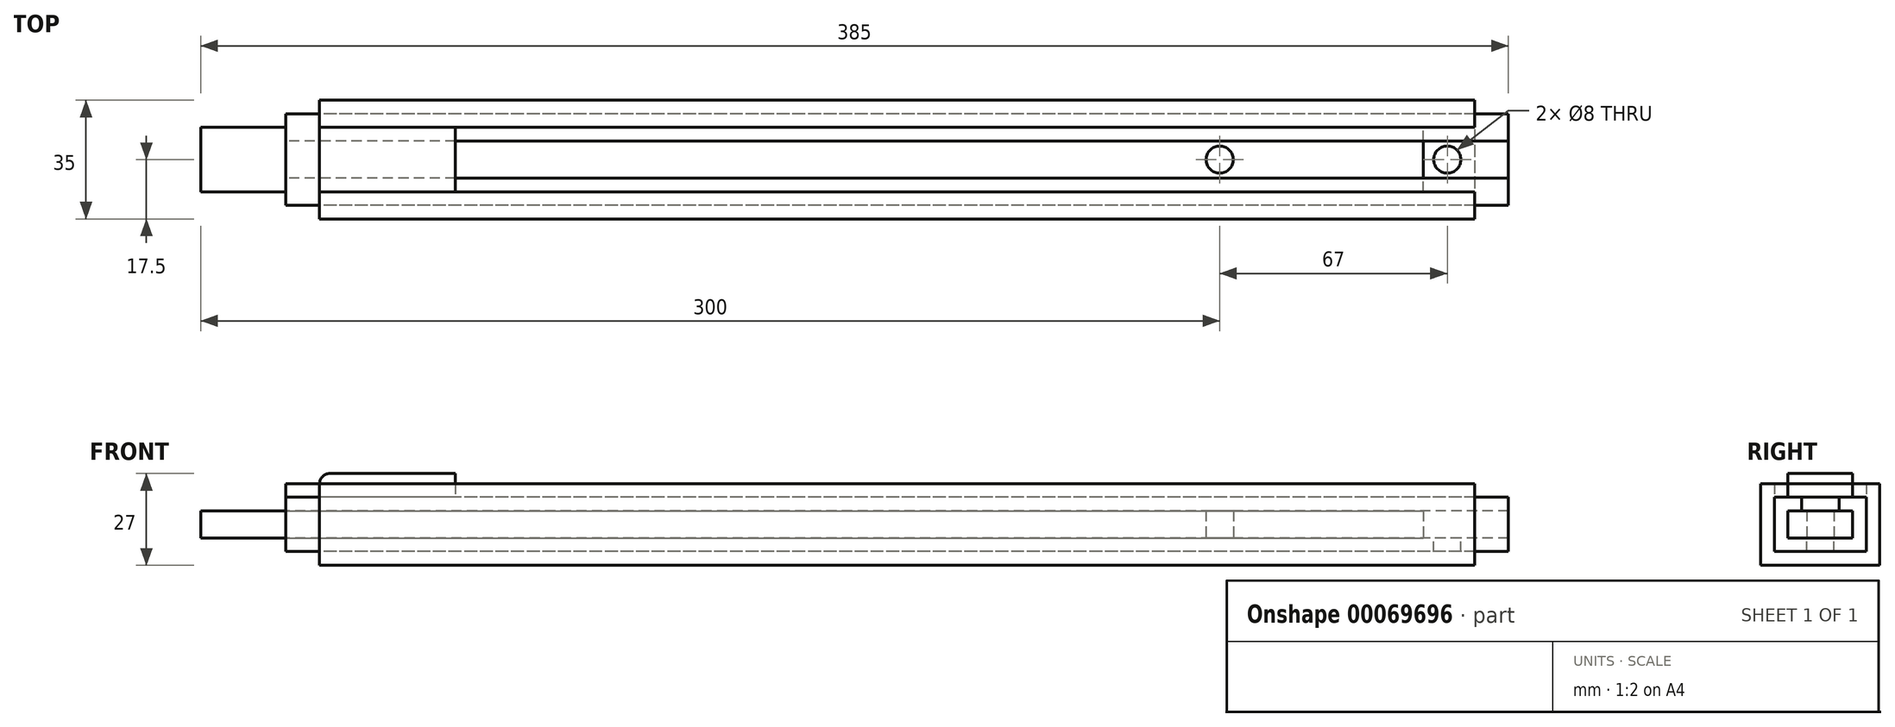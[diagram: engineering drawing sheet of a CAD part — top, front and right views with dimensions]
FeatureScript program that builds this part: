
annotation { "Feature Type Name" : "Feature", "Feature Type Description" : "" }
export const myFeature = defineFeature(function(context is Context, id is Id, definition is map)
    precondition{}
    {
        {
            var Q0;
            Q0=qCreatedBy(makeId("Top.planeOp"),FACE);
            var sketch = newSketch(context, id + "F0", { "sketchPlane" : qUnion([Q0])});
            skLineSegment(sketch, "E0.bottom", {"start": v(0, 0) * mm, "end": v(360, 0) * mm});
            skLineSegment(sketch, "E0.top", {"start": v(0, 19) * mm, "end": v(360, 19) * mm});
            skLineSegment(sketch, "E0.left", {"start": v(0, 0) * mm, "end": v(0, 19) * mm});
            skLineSegment(sketch, "E0.right", {"start": v(360, 0) * mm, "end": v(360, 19) * mm});
            skCircle(sketch, "E1", {"center": v(300, 9.5) * mm, "radius": 4 * mm});
            skPoint(sketch, "E1.centerSnap0", {"position": v(360, 9.5) * mm});
            skSolve(sketch);
        }
        {
            var Q0;
            Q0=makeQuery(id+"F0.imprint","IMPRINT",FACE,{"disambiguationData":[TD([[makeQuery(id+"F0.imprint","IMPRINT",EDGE,{"derivedFrom":sQuery(id+"F0.wireOp",EDGE,"E0.bottom")}),1.0]])]});
            extrude(context, id + "F1", {"entities" : qUnion([Q0]), "depth" : 8 * mm});
        }
        {
            var Q0;
            Q0=makeQuery(id+"F1.opExtrude","SWEPT_FACE",FACE,{"disambiguationData":[OSD([sQuery(id+"F0.wireOp",EDGE,"E0.left")])]});
            cPlane(context, id + "F2", {"entities" : qUnion([Q0]), "cplaneType" : CPlaneType.OFFSET, "offset" : 25 * mm, "oppositeDirection" : true, "width" : 150 * mm, "height" : 150 * mm});
        }
        {
            var Q0;
            Q0=qCreatedBy(id+"F2.planeOp",FACE);
            var sketch = newSketch(context, id + "F3", { "sketchPlane" : qUnion([Q0])});
            skLineSegment(sketch, "E2.0.0", {"start": v(-19, 0) * mm, "end": v(0, 0) * mm});
            skLineSegment(sketch, "E2.0.1", {"start": v(0, 0) * mm, "end": v(0, 8) * mm});
            skLineSegment(sketch, "E2.0.2", {"start": v(0, 8) * mm, "end": v(-19, 8) * mm});
            skLineSegment(sketch, "E2.0.3", {"start": v(-19, 8) * mm, "end": v(-19, 0) * mm});
            skLineSegment(sketch, "E3.bottom", {"start": v(-23, -4) * mm, "end": v(4, -4) * mm});
            skLineSegment(sketch, "E3.top", {"start": v(-23, 12) * mm, "end": v(-15, 12) * mm});
            skLineSegment(sketch, "E3.left", {"start": v(-23, -4) * mm, "end": v(-23, 12) * mm});
            skLineSegment(sketch, "E3.right", {"start": v(4, -4) * mm, "end": v(4, 12) * mm});
            skLineSegment(sketch, "E4", {"start": v(-15, 12) * mm, "end": v(-15, 8) * mm});
            skLineSegment(sketch, "E5", {"start": v(-4, 12) * mm, "end": v(-4, 8) * mm});
            skLineSegment(sketch, "E6.trimOffspring", {"start": v(-4, 12) * mm, "end": v(4, 12) * mm});
            skSolve(sketch);
        }
        {
            var Q0;
            Q0=makeQuery(id+"F3.imprint","IMPRINT",FACE,{"disambiguationData":[TD([[makeQuery(id+"F3.imprint","IMPRINT",EDGE,{"derivedFrom":sQuery(id+"F3.wireOp",EDGE,"E2.0.0")}),-1.0]])]});
            extrude(context, id + "F4", {"entities" : qUnion([Q0]), "oppositeDirection" : true, "depth" : 360 * mm});
        }
        {
            var Q0;
            Q0=makeQuery(id+"F4.opExtrude","CAP_FACE",FACE,{"disambiguationData":[OSD([sQuery(id+"F3.wireOp",EDGE,"E2.0.0"),sQuery(id+"F3.wireOp",EDGE,"E2.0.1"),sQuery(id+"F3.wireOp",EDGE,"E2.0.2"),sQuery(id+"F3.wireOp",EDGE,"E2.0.3"),sQuery(id+"F3.wireOp",EDGE,"E3.bottom"),sQuery(id+"F3.wireOp",EDGE,"E3.top"),sQuery(id+"F3.wireOp",EDGE,"E3.left"),sQuery(id+"F3.wireOp",EDGE,"E3.right"),sQuery(id+"F3.wireOp",EDGE,"E4"),sQuery(id+"F3.wireOp",EDGE,"E5"),sQuery(id+"F3.wireOp",EDGE,"E6.trimOffspring")])],"isStart":true});
            cPlane(context, id + "F5", {"entities" : qUnion([Q0]), "cplaneType" : CPlaneType.OFFSET, "offset" : 10 * mm, "oppositeDirection" : true, "width" : 150 * mm, "height" : 150 * mm});
        }
        {
            var Q0;
            Q0=qCreatedBy(id+"F5.planeOp",FACE);
            var sketch = newSketch(context, id + "F6", { "sketchPlane" : qUnion([Q0])});
            skLineSegment(sketch, "E7.bottom", {"start": v(-27, -8) * mm, "end": v(8, -8) * mm});
            skLineSegment(sketch, "E7.top", {"start": v(-27, 16) * mm, "end": v(-19, 16) * mm});
            skLineSegment(sketch, "E7.left", {"start": v(-27, -8) * mm, "end": v(-27, 16) * mm});
            skLineSegment(sketch, "E7.right", {"start": v(8, -8) * mm, "end": v(8, 16) * mm});
            skLineSegment(sketch, "E8", {"start": v(0, 16) * mm, "end": v(0, 11.98) * mm});
            skLineSegment(sketch, "E9.0", {"start": v(-19, 8) * mm, "end": v(-19, 0) * mm});
            skLineSegment(sketch, "E10", {"start": v(-19, 16) * mm, "end": v(-19, 11.9) * mm});
            skLineSegment(sketch, "E11.trimOffspring", {"start": v(0, 16) * mm, "end": v(8, 16) * mm});
            skLineSegment(sketch, "E12.0", {"start": v(-23, -4) * mm, "end": v(-23, 12) * mm});
            skLineSegment(sketch, "E13.0", {"start": v(-23, 12) * mm, "end": v(-15, 12) * mm});
            skLineSegment(sketch, "E14.0", {"start": v(-23, -4) * mm, "end": v(4, -4) * mm});
            skLineSegment(sketch, "E15.0", {"start": v(4, -4) * mm, "end": v(4, 12) * mm});
            skLineSegment(sketch, "E16.0", {"start": v(-4, 12) * mm, "end": v(4, 12) * mm});
            skSolve(sketch);
        }
        {
            var Q0;
            Q0=makeQuery(id+"F6.imprint","IMPRINT",FACE,{"disambiguationData":[TD([[makeQuery(id+"F6.imprint","IMPRINT",EDGE,{"derivedFrom":sQuery(id+"F6.wireOp",EDGE,"E7.bottom")}),1.0]])]});
            extrude(context, id + "F7", {"entities" : qUnion([Q0]), "oppositeDirection" : true, "depth" : 340 * mm});
        }
        {
            var Q0;
            Q0=makeQuery(id+"F4.opExtrude","SWEPT_FACE",FACE,{"disambiguationData":[OSD([sQuery(id+"F3.wireOp",EDGE,"E3.top")])]});
            var sketch = newSketch(context, id + "F8", { "sketchPlane" : qUnion([Q0])});
            skLineSegment(sketch, "E17.0.0", {"start": v(25, 23) * mm, "end": v(25, 15) * mm});
            skLineSegment(sketch, "E17.0.1", {"start": v(25, 15) * mm, "end": v(385, 15) * mm});
            skLineSegment(sketch, "E17.0.2", {"start": v(385, 15) * mm, "end": v(385, 23) * mm});
            skLineSegment(sketch, "E17.0.3", {"start": v(385, 23) * mm, "end": v(25, 23) * mm});
            skLineSegment(sketch, "E18.0.0", {"start": v(25, 4) * mm, "end": v(25, -4) * mm});
            skLineSegment(sketch, "E18.0.1", {"start": v(25, -4) * mm, "end": v(385, -4) * mm});
            skLineSegment(sketch, "E18.0.2", {"start": v(385, -4) * mm, "end": v(385, 4) * mm});
            skLineSegment(sketch, "E18.0.3", {"start": v(385, 4) * mm, "end": v(25, 4) * mm});
            skLineSegment(sketch, "E19.0.0", {"start": v(35, 0) * mm, "end": v(35, -8) * mm});
            skLineSegment(sketch, "E19.0.1", {"start": v(35, -8) * mm, "end": v(375, -8) * mm});
            skLineSegment(sketch, "E19.0.2", {"start": v(375, -8) * mm, "end": v(375, 0) * mm});
            skLineSegment(sketch, "E19.0.3", {"start": v(375, 0) * mm, "end": v(35, 0) * mm});
            skLineSegment(sketch, "E20.0.0", {"start": v(35, 27) * mm, "end": v(35, 19) * mm});
            skLineSegment(sketch, "E20.0.1", {"start": v(35, 19) * mm, "end": v(375, 19) * mm});
            skLineSegment(sketch, "E20.0.2", {"start": v(375, 19) * mm, "end": v(375, 27) * mm});
            skLineSegment(sketch, "E20.0.3", {"start": v(375, 27) * mm, "end": v(35, 27) * mm});
            skLineSegment(sketch, "E21", {"start": v(75, 19) * mm, "end": v(75, 0) * mm});
            skLineSegment(sketch, "E22", {"start": v(25, 15) * mm, "end": v(25, 4) * mm});
            skSolve(sketch);
        }
        {
            var Q0;
            {var subQ5=sQuery(id+"F8.wireOp",EDGE,"E17.0.0");Q0=makeQuery(id+"F8.imprint","IMPRINT",FACE,{"disambiguationData":[TD([[makeQuery(id+"F8.imprint","IMPRINT",EDGE,{"derivedFrom":subQ5}),1.0]])]});}
            var Q1;
            {var subQ0=sQuery(id+"F8.wireOp",EDGE,"E22");Q1=makeQuery(id+"F8.imprint","IMPRINT",FACE,{"disambiguationData":[TD([[makeQuery(id+"F8.imprint","IMPRINT",EDGE,{"derivedFrom":subQ0}),1.0]])]});}
            var Q2;
            {var subQ6=sQuery(id+"F8.wireOp",EDGE,"E18.0.0");Q2=makeQuery(id+"F8.imprint","IMPRINT",FACE,{"disambiguationData":[TD([[makeQuery(id+"F8.imprint","IMPRINT",EDGE,{"derivedFrom":subQ6}),1.0]])]});}
            extrude(context, id + "F9", {"entities" : qUnion([Q0, Q1, Q2]), "depth" : 4 * mm});
        }
        {
            var Q0;
            Q0=makeQuery(id+"F7.opExtrude","SWEPT_FACE",FACE,{"disambiguationData":[OSD([sQuery(id+"F6.wireOp",EDGE,"E7.top")])]});
            var sketch = newSketch(context, id + "F10", { "sketchPlane" : qUnion([Q0])});
            skLineSegment(sketch, "E23.0.0", {"start": v(35, 27) * mm, "end": v(35, 19) * mm});
            skLineSegment(sketch, "E23.0.1", {"start": v(35, 19) * mm, "end": v(375, 19) * mm});
            skLineSegment(sketch, "E23.0.2", {"start": v(375, 19) * mm, "end": v(375, 27) * mm});
            skLineSegment(sketch, "E23.0.3", {"start": v(375, 27) * mm, "end": v(35, 27) * mm});
            skLineSegment(sketch, "E24.0.0", {"start": v(35, 0) * mm, "end": v(35, -8) * mm});
            skLineSegment(sketch, "E24.0.1", {"start": v(35, -8) * mm, "end": v(375, -8) * mm});
            skLineSegment(sketch, "E24.0.2", {"start": v(375, -8) * mm, "end": v(375, 0) * mm});
            skLineSegment(sketch, "E24.0.3", {"start": v(375, 0) * mm, "end": v(35, 0) * mm});
            skLineSegment(sketch, "E25.0", {"start": v(75, 19) * mm, "end": v(75, 0) * mm});
            skLineSegment(sketch, "E26.bottom", {"start": v(35, -8) * mm, "end": v(75, -8) * mm});
            skLineSegment(sketch, "E26.top", {"start": v(35, 27) * mm, "end": v(75, 27) * mm});
            skLineSegment(sketch, "E26.left", {"start": v(35, -8) * mm, "end": v(35, 27) * mm});
            skLineSegment(sketch, "E26.right", {"start": v(75, -8) * mm, "end": v(75, 27) * mm});
            skSolve(sketch);
        }
        {
            var Q0;
            {var subQ5=sQuery(id+"F10.wireOp",EDGE,"E26.top");Q0=makeQuery(id+"F10.imprint","IMPRINT",FACE,{"disambiguationData":[TD([[makeQuery(id+"F10.imprint","IMPRINT",EDGE,{"derivedFrom":subQ5}),1.0]])]});}
            var Q1;
            {var subQ0=sQuery(id+"F10.wireOp",EDGE,"E26.left");var subQ1=sQuery(id+"F10.wireOp",EDGE,"E23.0.1");var subQ2=makeQuery(id+"F10.imprint","INTERSECT",VERTEX,{"derivedFrom":[subQ1,subQ0]});Q1=makeQuery(id+"F10.imprint","IMPRINT",FACE,{"disambiguationData":[TD([[makeQuery(id+"F10.imprint","IMPRINT",EDGE,{"disambiguationData":[TD([[subQ2,1.0]])],"derivedFrom":subQ1}),1.0]])]});}
            var Q2;
            {var subQ5=sQuery(id+"F10.wireOp",EDGE,"E26.bottom");Q2=makeQuery(id+"F10.imprint","IMPRINT",FACE,{"disambiguationData":[TD([[makeQuery(id+"F10.imprint","IMPRINT",EDGE,{"derivedFrom":subQ5}),1.0]])]});}
            extrude(context, id + "F11", {"entities" : qUnion([Q0, Q1, Q2]), "depth" : 3 * mm});
        }
        {
            var Q0;
            Q0=makeQuery(id+"F11.opExtrude","CAP_EDGE",EDGE,{"disambiguationData":[OSD([sQuery(id+"F10.wireOp",EDGE,"E26.bottom")])],"isStart":false});
            var Q1;
            Q1=makeQuery(id+"F11.opExtrude","CAP_EDGE",EDGE,{"disambiguationData":[OSD([sQuery(id+"F10.wireOp",EDGE,"E26.left")])],"isStart":false});
            var Q2;
            Q2=makeQuery(id+"F11.opExtrude","CAP_EDGE",EDGE,{"disambiguationData":[OSD([sQuery(id+"F10.wireOp",EDGE,"E26.top")])],"isStart":false});
            var Q3;
            Q3=makeQuery(id+"F11.opExtrude","CAP_EDGE",EDGE,{"disambiguationData":[OSD([sQuery(id+"F10.wireOp",EDGE,"E26.right")])],"isStart":false});
            fillet(context, id + "F12", {"entities" : qUnion([Q0, Q1, Q2, Q3]), "radius" : 3 * mm, "tangentPropagation" : true, "allowEdgeOverflow" : false});
        }
        {
            var Q0;
            Q0=makeQuery(id+"F4.opExtrude","SWEPT_FACE",FACE,{"disambiguationData":[OSD([sQuery(id+"F3.wireOp",EDGE,"E2.0.0")])]});
            var sketch = newSketch(context, id + "F13", { "sketchPlane" : qUnion([Q0])});
            skCircle(sketch, "E27", {"center": v(367, 9.5) * mm, "radius": 4 * mm});
            skPoint(sketch, "E27.centerSnap0", {"position": v(385, 9.5) * mm});
            skSolve(sketch);
        }
        {
            var Q0;
            Q0=makeQuery(id+"F13.imprint","IMPRINT",FACE,{"disambiguationData":[TD([[makeQuery(id+"F13.imprint","IMPRINT",EDGE,{"derivedFrom":sQuery(id+"F13.wireOp",EDGE,"E27")}),1.0]])]});
            extrude(context, id + "F14", {"entities" : qUnion([Q0]), "operationType" : NewBodyOperationType.REMOVE, "oppositeDirection" : true, "depth" : 4 * mm});
        }
    });
